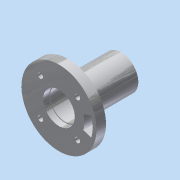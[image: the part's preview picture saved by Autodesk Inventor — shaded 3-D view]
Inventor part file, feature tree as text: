
AUTODESK INVENTOR PART (.ipt)
format: ipt  version: 2015 (Build 190159000, 159)  size: 138,240 bytes
history: native  units: in
note: dims shown in document units (in); Inventor stores cm internally (conversion verified against a paired STEP export)
features: sketch x2, other x1, revolve x1, extrude x1
ambient origin geometry x8: Origin, YZ Plane, XZ Plane, XY Plane, X Axis, Y Axis, Z Axis, Center Point
bodies: Solid1 (feature_tree)
feature tree (5):
  other  "Stator.ipt"
  sketch  "Sketch1"  dims[d0=0.9843in d1=0.25in]
  revolve  "Revolution1"  [1 undecoded]
  extrude  "Extrusion1"  Depth=1.378in
  sketch  "Sketch2"  dims[d3=0.3937in d4=1.378in d5=0.1575in d6=0.1575in d7=0.4134in d9=0.0197in d10=90.0deg d11=0.4528in d12=0.1378in d15=45.0deg d17=1.5748in d19=360.0deg d21=1.0in d22=0.0in]
note: 1 required parameter value undecoded (feature->parameter linkage not recoverable at this tier; creation-order binding heuristic only, values carry confidence <= 0.55)
